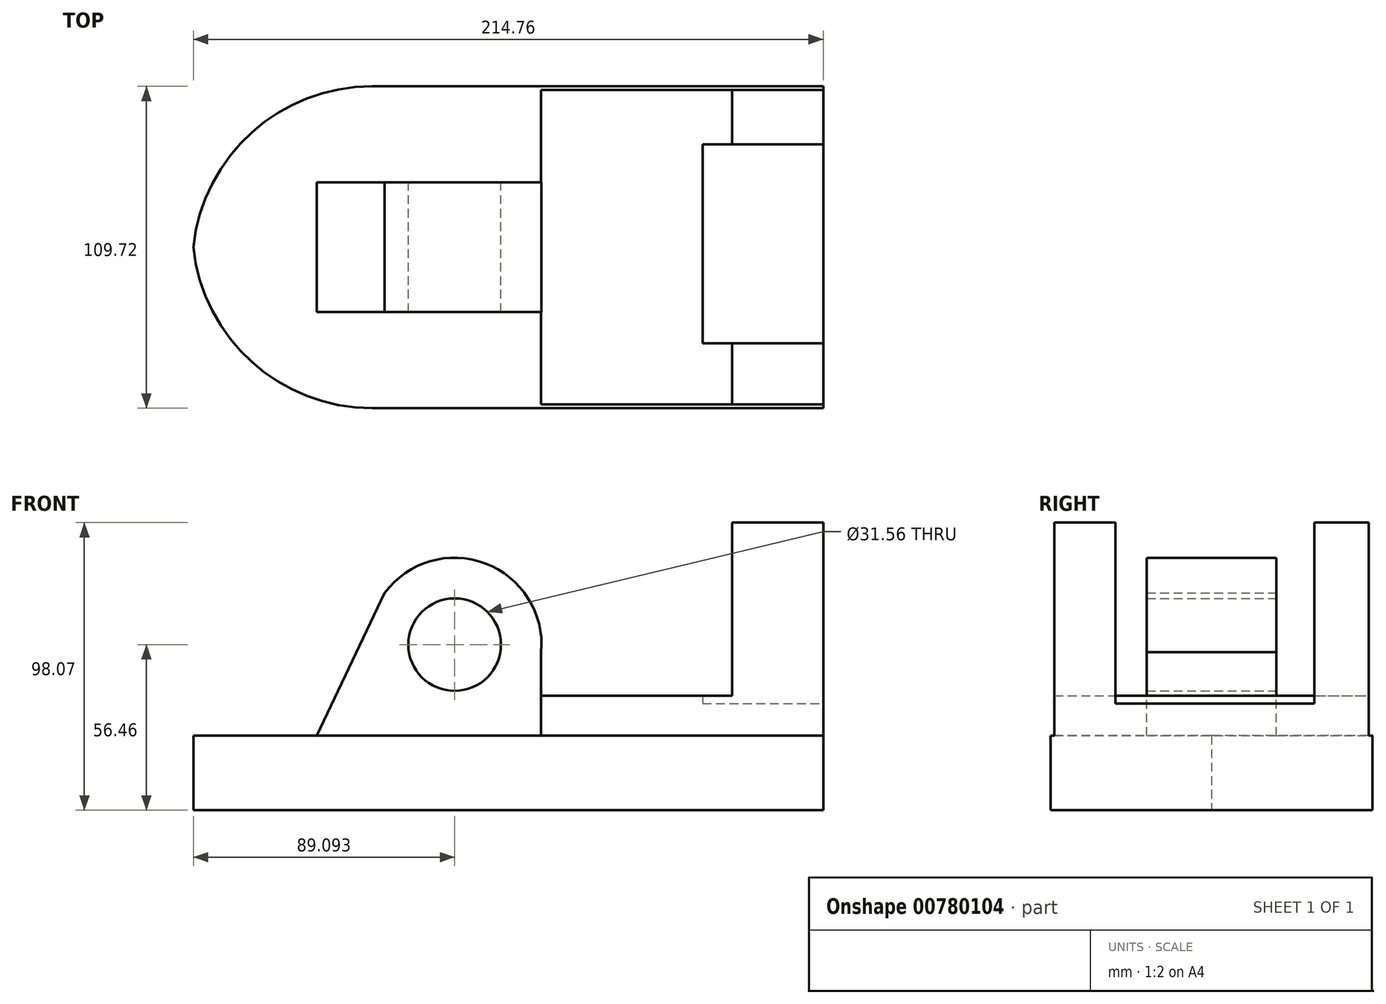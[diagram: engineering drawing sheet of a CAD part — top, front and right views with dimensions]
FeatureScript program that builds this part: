
annotation { "Feature Type Name" : "Feature", "Feature Type Description" : "" }
export const myFeature = defineFeature(function(context is Context, id is Id, definition is map)
    precondition{}
    {
        {
            var Q0;
            Q0=qCreatedBy(makeId("Front.planeOp"),FACE);
            var sketch = newSketch(context, id + "F0", { "sketchPlane" : qUnion([Q0])});
            skLineSegment(sketch, "E0", {"start": v(-107.46, 0) * mm, "end": v(107.64, 0) * mm});
            skLineSegment(sketch, "E1", {"start": v(107.64, 0) * mm, "end": v(107.64, 98.07) * mm});
            skLineSegment(sketch, "E2", {"start": v(107.64, 98.07) * mm, "end": v(76.64, 98.07) * mm});
            skLineSegment(sketch, "E3", {"start": v(76.64, 98.07) * mm, "end": v(76.64, 39.04) * mm});
            skLineSegment(sketch, "E4", {"start": v(76.64, 39.04) * mm, "end": v(11.48, 39.04) * mm});
            skLineSegment(sketch, "E5", {"start": v(11.48, 39.04) * mm, "end": v(11.48, 53.9) * mm});
            skLineSegment(sketch, "E6", {"start": v(-107.46, 0) * mm, "end": v(-107.46, 25.4) * mm});
            skLineSegment(sketch, "E7", {"start": v(-107.46, 25.4) * mm, "end": v(-65.07, 25.4) * mm});
            skLineSegment(sketch, "E8", {"start": v(-65.07, 25.4) * mm, "end": v(-41.86, 74.04) * mm});
            skArc(sketch, "E9", {"start": v(11.48, 53.9) * mm, "mid": v(-13, 85.65) * mm, "end": v(-46.7, 63.92) * mm});
            skLineSegment(sketch, "E10", {"start": v(-41.86, 74.04) * mm, "end": v(11.48, 53.9) * mm, "construction": true});
            skLineSegment(sketch, "E11", {"start": v(-65.07, 25.4) * mm, "end": v(107.64, 25.4) * mm});
            skLineSegment(sketch, "E12", {"start": v(11.48, 39.04) * mm, "end": v(11.48, 25.4) * mm});
            skCircle(sketch, "E13", {"center": v(-18.03, 56.46) * mm, "radius": 15.78 * mm});
            skSolve(sketch);
        }
        {
            var Q0;
            {var subQ2=sQuery(id+"F0.wireOp",EDGE,"E0");Q0=makeQuery(id+"F0.imprint","IMPRINT",FACE,{"disambiguationData":[TD([[makeQuery(id+"F0.imprint","IMPRINT",EDGE,{"derivedFrom":subQ2}),1.0]])]});}
            extrude(context, id + "F1", {"entities" : qUnion([Q0]), "endBound" : BoundingType.SYMMETRIC, "depth" : 109.73 * mm, "offsetDistance" : 25.4 * mm});
        }
        {
            var Q0;
            {var subQ6=sQuery(id+"F0.wireOp",EDGE,"E5");Q0=makeQuery(id+"F0.imprint","IMPRINT",FACE,{"disambiguationData":[TD([[makeQuery(id+"F0.imprint","IMPRINT",EDGE,{"derivedFrom":subQ6}),1.0]])]});}
            extrude(context, id + "F2", {"entities" : qUnion([Q0]), "operationType" : NewBodyOperationType.ADD, "endBound" : BoundingType.SYMMETRIC, "depth" : 44.2 * mm, "offsetDistance" : 25.4 * mm});
        }
        {
            var Q0;
            {var subQ1=sQuery(id+"F0.wireOp",EDGE,"E2");Q0=makeQuery(id+"F0.imprint","IMPRINT",FACE,{"disambiguationData":[TD([[makeQuery(id+"F0.imprint","IMPRINT",EDGE,{"derivedFrom":subQ1}),1.0]])]});}
            extrude(context, id + "F3", {"entities" : qUnion([Q0]), "operationType" : NewBodyOperationType.ADD, "endBound" : BoundingType.SYMMETRIC, "depth" : 107.19 * mm, "offsetDistance" : 25.4 * mm});
        }
        {
            var Q0;
            Q0=makeQuery(id+"F1.opExtrude","CAP_EDGE",EDGE,{"disambiguationData":[OSD([sQuery(id+"F0.wireOp",EDGE,"E6")])],"isStart":true});
            var Q1;
            Q1=makeQuery(id+"F1.opExtrude","CAP_EDGE",EDGE,{"disambiguationData":[OSD([sQuery(id+"F0.wireOp",EDGE,"E6")])],"isStart":false});
            fillet(context, id + "F4", {"entities" : qUnion([Q0, Q1]), "radius" : 61.32 * mm, "tangentPropagation" : true, "allowEdgeOverflow" : false});
        }
        {
            var Q0;
            Q0=makeQuery(id+"F0.imprint","IMPRINT",FACE,{"disambiguationData":[TD([[makeQuery(id+"F0.imprint","IMPRINT",EDGE,{"derivedFrom":sQuery(id+"F0.wireOp",EDGE,"E13")}),1.0]])]});
            extrude(context, id + "F5", {"entities" : qUnion([Q0]), "operationType" : NewBodyOperationType.REMOVE, "oppositeDirection" : true, "depth" : 131.83 * mm, "offsetDistance" : 25.4 * mm});
        }
        {
            var Q0;
            {var subQ0=sQuery(id+"F0.wireOp",EDGE,"E1");Q0=makeQuery(id+"F3.boolean.opBoolean","MERGE",FACE,{"derivedFrom":[makeQuery(id+"F1.opExtrude","SWEPT_FACE",FACE,{"disambiguationData":[OSD([subQ0])]}),makeQuery(id+"F3.opExtrude","SWEPT_FACE",FACE,{"disambiguationData":[OSD([subQ0])]})]});}
            var sketch = newSketch(context, id + "F6", { "sketchPlane" : qUnion([Q0])});
            skLineSegment(sketch, "E14", {"start": v(-32.75, 98.07) * mm, "end": v(-32.75, 36.31) * mm});
            skLineSegment(sketch, "E15", {"start": v(-32.75, 36.31) * mm, "end": v(35.05, 36.31) * mm});
            skLineSegment(sketch, "E16", {"start": v(35.05, 36.31) * mm, "end": v(35.05, 98.07) * mm});
            skSolve(sketch);
        }
        {
            var Q0;
            {var subQ0=sQuery(id+"F6.wireOp",EDGE,"E14");Q0=makeQuery(id+"F6.imprint","IMPRINT",FACE,{"disambiguationData":[TD([[makeQuery(id+"F6.imprint","IMPRINT",EDGE,{"derivedFrom":subQ0}),1.0]])]});}
            extrude(context, id + "F7", {"entities" : qUnion([Q0]), "operationType" : NewBodyOperationType.REMOVE, "oppositeDirection" : true, "depth" : 41.15 * mm, "offsetDistance" : 25.4 * mm});
        }
    });
